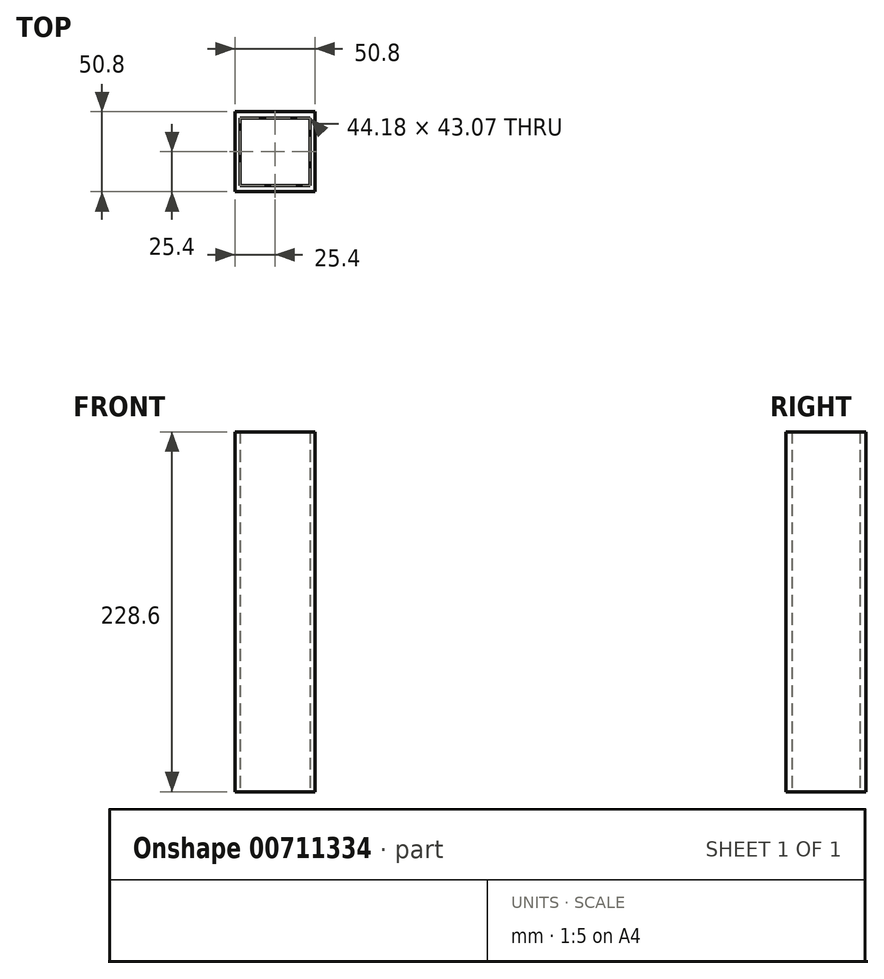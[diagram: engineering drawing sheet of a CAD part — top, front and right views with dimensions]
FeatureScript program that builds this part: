
annotation { "Feature Type Name" : "Feature", "Feature Type Description" : "" }
export const myFeature = defineFeature(function(context is Context, id is Id, definition is map)
    precondition{}
    {
        {
            var Q0;
            Q0=qCreatedBy(makeId("Top.planeOp"),FACE);
            var sketch = newSketch(context, id + "F0", { "sketchPlane" : qUnion([Q0])});
            skLineSegment(sketch, "E0.bottom", {"start": v(25.4, 25.4) * mm, "end": v(-25.4, 25.4) * mm});
            skLineSegment(sketch, "E0.top", {"start": v(25.4, -25.4) * mm, "end": v(-25.4, -25.4) * mm});
            skLineSegment(sketch, "E0.left", {"start": v(25.4, 25.4) * mm, "end": v(25.4, -25.4) * mm});
            skLineSegment(sketch, "E0.right", {"start": v(-25.4, 25.4) * mm, "end": v(-25.4, -25.4) * mm});
            skPoint(sketch, "E0.middle", {"position": v(0, 0) * mm});
            skLineSegment(sketch, "E1.bottom", {"start": v(22.1, 21.53) * mm, "end": v(-22.1, 21.53) * mm});
            skLineSegment(sketch, "E1.top", {"start": v(22.1, -21.53) * mm, "end": v(-22.1, -21.53) * mm});
            skLineSegment(sketch, "E1.left", {"start": v(22.1, 21.53) * mm, "end": v(22.1, -21.53) * mm});
            skLineSegment(sketch, "E1.right", {"start": v(-22.1, 21.53) * mm, "end": v(-22.1, -21.53) * mm});
            skSolve(sketch);
        }
        {
            var Q0;
            Q0=makeQuery(id+"F0.imprint","IMPRINT",FACE,{"disambiguationData":[TD([[makeQuery(id+"F0.imprint","IMPRINT",EDGE,{"derivedFrom":sQuery(id+"F0.wireOp",EDGE,"E0.bottom")}),1.0]])]});
            extrude(context, id + "F1", {"entities" : qUnion([Q0]), "depth" : 228.6 * mm, "offsetDistance" : 25.4 * mm});
        }
    });
